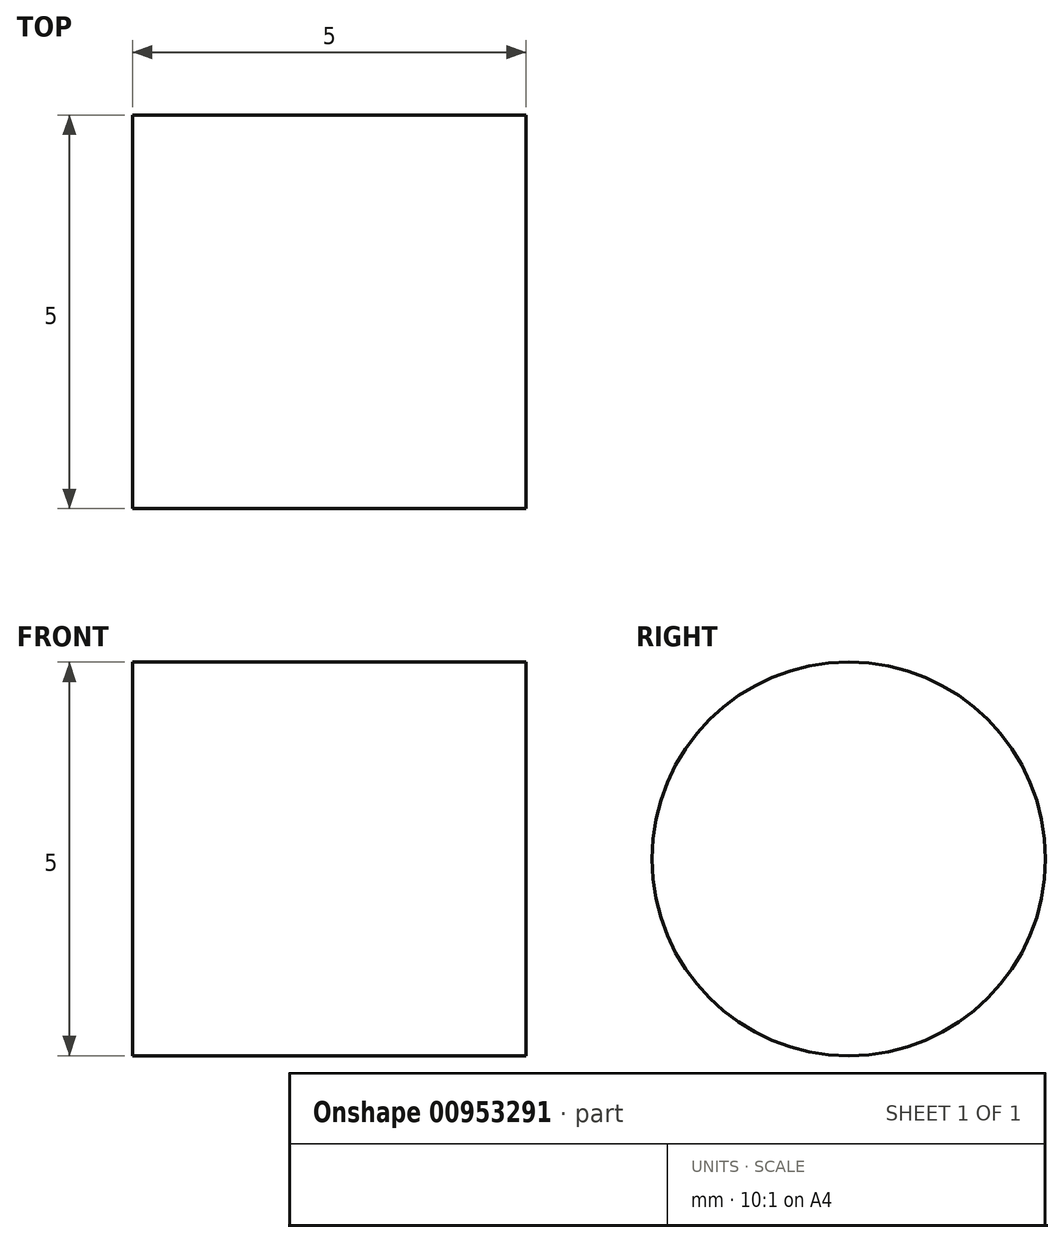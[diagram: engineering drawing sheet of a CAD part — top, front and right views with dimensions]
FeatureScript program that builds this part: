
annotation { "Feature Type Name" : "Feature", "Feature Type Description" : "" }
export const myFeature = defineFeature(function(context is Context, id is Id, definition is map)
    precondition{}
    {
        {
            var Q0;
            Q0=qCreatedBy(makeId("Right.planeOp"),FACE);
            var sketch = newSketch(context, id + "F0", { "sketchPlane" : qUnion([Q0])});
            skCircle(sketch, "E0", {"center": v(0, 0) * mm, "radius": 2.5 * mm});
            skSolve(sketch);
        }
        {
            var Q0;
            Q0 = qSketchRegion(id + "F0", true);
            extrude(context, id + "F1", {"entities" : qUnion([Q0]), "depth" : 5 * mm, "offsetDistance" : 25 * mm});
        }
    });
